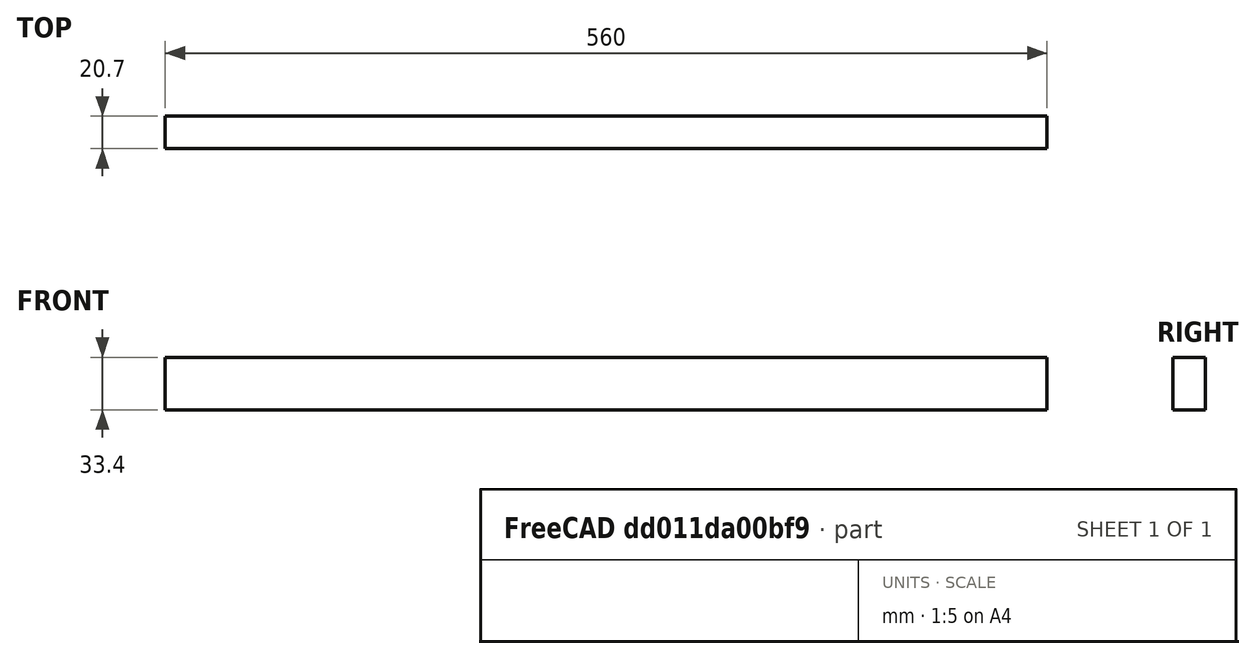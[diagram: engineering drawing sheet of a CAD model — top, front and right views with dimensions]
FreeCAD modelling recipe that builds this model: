
FCSTD DOCUMENT  (FreeCAD 0.22R34651 (Git))
Label: ULI-3865416
License: All rights reserved
LicenseURL: http://en.wikipedia.org/wiki/All_rights_reserved
objects: Sketcher::SketchObject×2, Spreadsheet::Sheet×1, PartDesign::SubShapeBinder×1, PartDesign::Pad×1, PartDesign::Body×1
note: 6 computed .brp shape members not serialized (recipe doc carries the construction recipe); baked Part::Feature solids carry a one-line shape summary decoded from their .brp

FEATURE [Sketcher::SketchObject] Sketch
  FullyConstrained = true
  expr: Constraints[11] = <<Properties>>.width
  sketch-geometry (5):
    g0: LineSegment StartX=-280 StartY=-10.35 StartZ=0 EndX=-280 EndY=10.35 EndZ=0
    g1: LineSegment StartX=-280 StartY=10.35 StartZ=0 EndX=280 EndY=10.35 EndZ=0
    g2: LineSegment StartX=280 StartY=10.35 StartZ=0 EndX=280 EndY=-10.35 EndZ=0
    g3: LineSegment StartX=280 StartY=-10.35 StartZ=0 EndX=-280 EndY=-10.35 EndZ=0
    g4: GeomPoint X=0 Y=0 Z=0
  constraints (12):
    c: Coincident(g0,g1)
    c: Coincident(g1,g2)
    c: Coincident(g2,g3)
    c: Coincident(g3,g0)
    c: Horizontal(g1)
    c: Horizontal(g3)
    c: Vertical(g0)
    c: Vertical(g2)
    c: Symmetric(g1,g0,g4)
    c: Coincident(g4,g-1)
    c: DistanceX(g0,g1) = 560
    c: DistanceY(g0,g1) = 20.7
FEATURE [Sketcher::SketchObject] Sketch001
  FullyConstrained = true
  expr: Constraints[11] = <<Properties>>.width
  expr: Constraints[12] = <<Properties>>.height
  sketch-geometry (5):
    g0: LineSegment StartX=-10.35 StartY=33.4 StartZ=0 EndX=-10.35 EndY=0 EndZ=0
    g1: LineSegment StartX=-10.35 StartY=0 StartZ=0 EndX=10.35 EndY=0 EndZ=0
    g2: LineSegment StartX=10.35 StartY=0 StartZ=0 EndX=10.35 EndY=33.4 EndZ=0
    g3: LineSegment StartX=10.35 StartY=33.4 StartZ=0 EndX=-10.35 EndY=33.4 EndZ=0
    g4: GeomPoint X=0 Y=16.7 Z=0
  constraints (13):
    c: Coincident(g0,g1)
    c: Coincident(g1,g2)
    c: Coincident(g2,g3)
    c: Coincident(g3,g0)
    c: Horizontal(g1)
    c: Horizontal(g3)
    c: Vertical(g0)
    c: Vertical(g2)
    c: Symmetric(g1,g0,g4)
    c: PointOnObject(g4,g-2)
    c: PointOnObject(g1,g-1)
    c: DistanceX(g1,g1) = 20.7
    c: DistanceY(g2,g2) = 33.4
FEATURE [Spreadsheet::Sheet] Spreadsheet  label="Properties"
  cells = B2(length)==560 mm; C2(width)==20.7 mm; D2(height)==33.4 mm; E2(base_height)==22 mm; F2(light_height)==height - base_height
FEATURE [PartDesign::SubShapeBinder] Binder
  BindCopyOnChange = 0
  BindMode = 0
  ClaimChildren = false
  Context = -> Body [Binder.]
  Fuse = false
  MakeFace = true
  OffsetFill = false
  OffsetIntersection = false
  OffsetJoinType = 0
  OffsetOpenResult = false
  PartialLoad = false
  Placement = pos=(0,0,0) rot=(0.57735,0.57735,0.57735;2.0944rad)
  Relative = true
  Support = -> [Sketch001]
  _Version = 2
FEATURE [PartDesign::Pad] Pad
  Direction = (1,-2e-16,2e-16)
  Length = 560
  Length2 = 10
  Midplane = true
  Placement = pos=(0,0,0) rot=(0.57735,0.57735,0.57735;2.0944rad)
  Profile = -> Binder
  Type = 0
  expr: Length = <<Properties>>.length
FEATURE [PartDesign::Body] Body
  Group = -> [Binder,Pad]
  Origin = -> Origin
  Tip = -> Pad
